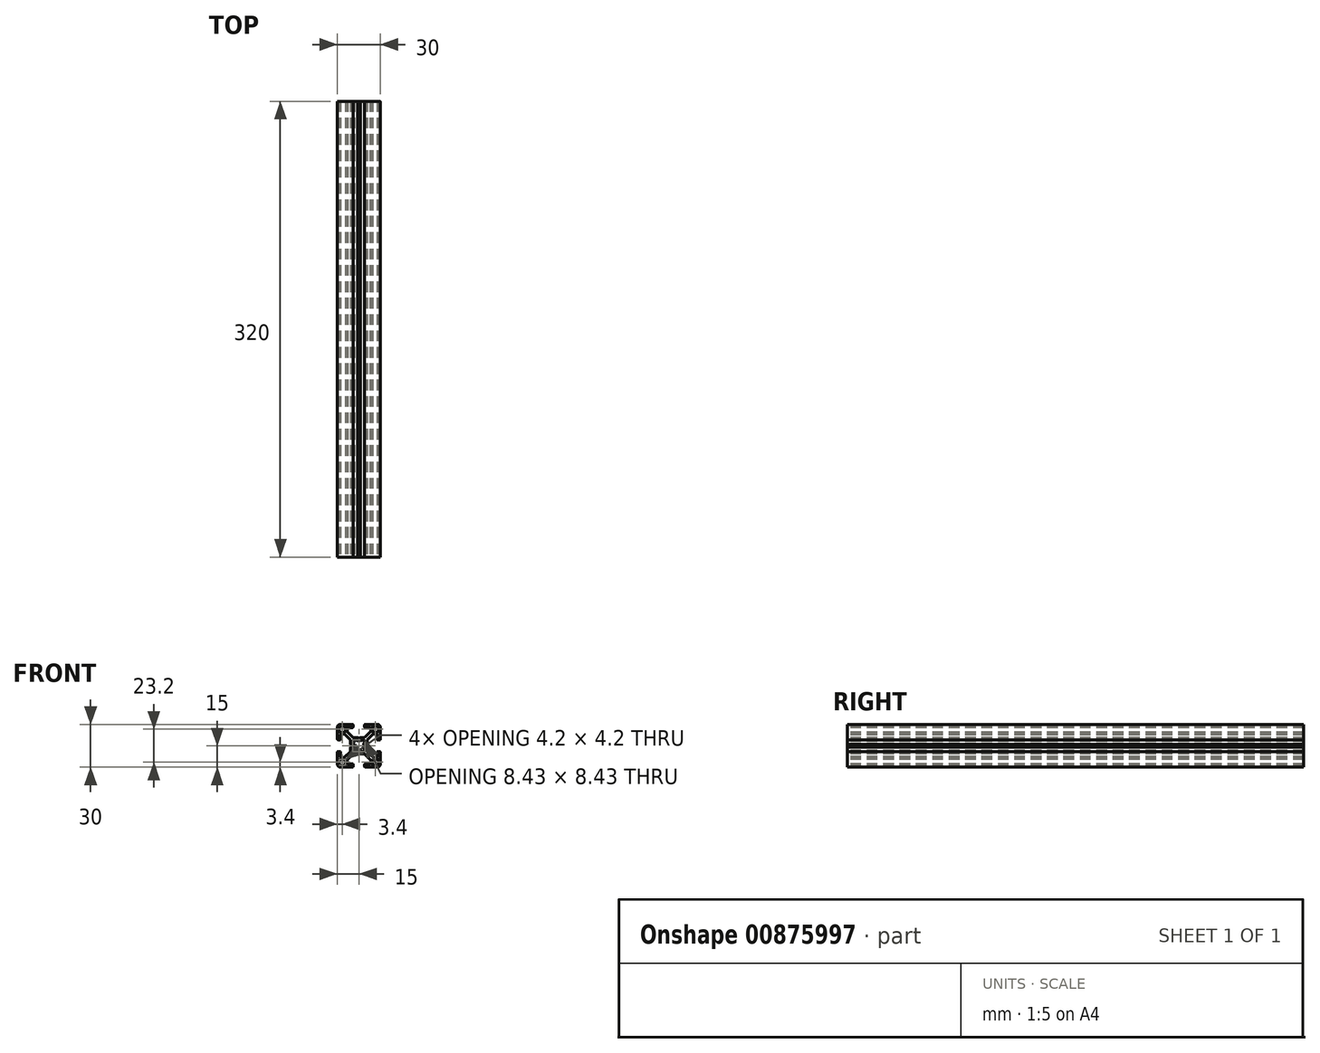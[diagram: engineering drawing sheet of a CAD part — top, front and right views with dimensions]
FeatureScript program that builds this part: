
annotation { "Feature Type Name" : "Feature", "Feature Type Description" : "" }
export const myFeature = defineFeature(function(context is Context, id is Id, definition is map)
    precondition{}
    {
        {
            var Q0;
            Q0=qCreatedBy(makeId("Front.planeOp"),FACE);
            var sketch = newSketch(context, id + "F0", { "sketchPlane" : qUnion([Q0])});
            skArc(sketch, "E0", {"start": v(9.88, 13.7) * mm, "mid": v(9.61, 13.59) * mm, "end": v(9.5, 13.32) * mm});
            skLineSegment(sketch, "E1", {"start": v(12.7, 13.7) * mm, "end": v(9.88, 13.7) * mm});
            skArc(sketch, "E2", {"start": v(13.7, 12.7) * mm, "mid": v(13.4, 13.4) * mm, "end": v(12.7, 13.7) * mm});
            skLineSegment(sketch, "E3", {"start": v(13.7, 9.88) * mm, "end": v(13.7, 12.7) * mm});
            skArc(sketch, "E4", {"start": v(13.32, 9.5) * mm, "mid": v(13.59, 9.61) * mm, "end": v(13.7, 9.88) * mm});
            skLineSegment(sketch, "E5", {"start": v(9.88, 9.5) * mm, "end": v(13.32, 9.5) * mm});
            skArc(sketch, "E6", {"start": v(9.5, 9.88) * mm, "mid": v(9.61, 9.61) * mm, "end": v(9.88, 9.5) * mm});
            skLineSegment(sketch, "E7", {"start": v(9.5, 13.32) * mm, "end": v(9.5, 9.88) * mm});
            skArc(sketch, "E8", {"start": v(-9.5, 13.32) * mm, "mid": v(-9.61, 13.59) * mm, "end": v(-9.88, 13.7) * mm});
            skLineSegment(sketch, "E9", {"start": v(-9.5, 9.88) * mm, "end": v(-9.5, 13.32) * mm});
            skArc(sketch, "E10", {"start": v(-9.88, 9.5) * mm, "mid": v(-9.61, 9.61) * mm, "end": v(-9.5, 9.88) * mm});
            skLineSegment(sketch, "E11", {"start": v(-13.32, 9.5) * mm, "end": v(-9.88, 9.5) * mm});
            skArc(sketch, "E12", {"start": v(-13.7, 9.88) * mm, "mid": v(-13.59, 9.61) * mm, "end": v(-13.32, 9.5) * mm});
            skLineSegment(sketch, "E13", {"start": v(-13.7, 12.7) * mm, "end": v(-13.7, 9.88) * mm});
            skArc(sketch, "E14", {"start": v(-12.7, 13.7) * mm, "mid": v(-13.4, 13.4) * mm, "end": v(-13.7, 12.7) * mm});
            skLineSegment(sketch, "E15", {"start": v(-9.88, 13.7) * mm, "end": v(-12.7, 13.7) * mm});
            skArc(sketch, "E16", {"start": v(-1.5, -3.2) * mm, "mid": v(0, -3.53) * mm, "end": v(1.5, -3.2) * mm});
            skLineSegment(sketch, "E17", {"start": v(-2.47, -3.98) * mm, "end": v(-1.5, -3.2) * mm});
            skArc(sketch, "E18", {"start": v(-3.98, -2.47) * mm, "mid": v(-3.9, -3.9) * mm, "end": v(-2.47, -3.98) * mm});
            skLineSegment(sketch, "E19", {"start": v(-3.2, -1.5) * mm, "end": v(-3.98, -2.47) * mm});
            skArc(sketch, "E20", {"start": v(-3.2, 1.5) * mm, "mid": v(-3.53, 0) * mm, "end": v(-3.2, -1.5) * mm});
            skLineSegment(sketch, "E21", {"start": v(-3.98, 2.47) * mm, "end": v(-3.2, 1.5) * mm});
            skArc(sketch, "E22", {"start": v(-2.47, 3.98) * mm, "mid": v(-3.9, 3.9) * mm, "end": v(-3.98, 2.47) * mm});
            skLineSegment(sketch, "E23", {"start": v(-1.5, 3.2) * mm, "end": v(-2.47, 3.98) * mm});
            skArc(sketch, "E24", {"start": v(1.5, 3.2) * mm, "mid": v(0, 3.53) * mm, "end": v(-1.5, 3.2) * mm});
            skLineSegment(sketch, "E25", {"start": v(2.47, 3.98) * mm, "end": v(1.5, 3.2) * mm});
            skArc(sketch, "E26", {"start": v(3.98, 2.47) * mm, "mid": v(3.9, 3.9) * mm, "end": v(2.47, 3.98) * mm});
            skLineSegment(sketch, "E27", {"start": v(3.2, 1.5) * mm, "end": v(3.98, 2.47) * mm});
            skArc(sketch, "E28", {"start": v(3.2, -1.5) * mm, "mid": v(3.53, 0) * mm, "end": v(3.2, 1.5) * mm});
            skLineSegment(sketch, "E29", {"start": v(3.98, -2.47) * mm, "end": v(3.2, -1.5) * mm});
            skArc(sketch, "E30", {"start": v(2.47, -3.98) * mm, "mid": v(3.9, -3.9) * mm, "end": v(3.98, -2.47) * mm});
            skLineSegment(sketch, "E31", {"start": v(1.5, -3.2) * mm, "end": v(2.47, -3.98) * mm});
            skArc(sketch, "E32", {"start": v(-13.32, -9.5) * mm, "mid": v(-13.59, -9.61) * mm, "end": v(-13.7, -9.88) * mm});
            skLineSegment(sketch, "E33", {"start": v(-9.88, -9.5) * mm, "end": v(-13.32, -9.5) * mm});
            skArc(sketch, "E34", {"start": v(-9.5, -9.88) * mm, "mid": v(-9.61, -9.61) * mm, "end": v(-9.88, -9.5) * mm});
            skLineSegment(sketch, "E35", {"start": v(-9.5, -13.32) * mm, "end": v(-9.5, -9.88) * mm});
            skArc(sketch, "E36", {"start": v(-9.88, -13.7) * mm, "mid": v(-9.61, -13.59) * mm, "end": v(-9.5, -13.32) * mm});
            skLineSegment(sketch, "E37", {"start": v(-12.7, -13.7) * mm, "end": v(-9.88, -13.7) * mm});
            skArc(sketch, "E38", {"start": v(-13.7, -12.7) * mm, "mid": v(-13.4, -13.4) * mm, "end": v(-12.7, -13.7) * mm});
            skLineSegment(sketch, "E39", {"start": v(-13.7, -9.88) * mm, "end": v(-13.7, -12.7) * mm});
            skArc(sketch, "E40", {"start": v(9.5, -13.32) * mm, "mid": v(9.61, -13.59) * mm, "end": v(9.88, -13.7) * mm});
            skLineSegment(sketch, "E41", {"start": v(9.5, -9.88) * mm, "end": v(9.5, -13.32) * mm});
            skArc(sketch, "E42", {"start": v(9.88, -9.5) * mm, "mid": v(9.61, -9.61) * mm, "end": v(9.5, -9.88) * mm});
            skLineSegment(sketch, "E43", {"start": v(13.32, -9.5) * mm, "end": v(9.88, -9.5) * mm});
            skArc(sketch, "E44", {"start": v(13.7, -9.88) * mm, "mid": v(13.59, -9.61) * mm, "end": v(13.32, -9.5) * mm});
            skLineSegment(sketch, "E45", {"start": v(13.7, -12.7) * mm, "end": v(13.7, -9.88) * mm});
            skArc(sketch, "E46", {"start": v(12.7, -13.7) * mm, "mid": v(13.4, -13.4) * mm, "end": v(13.7, -12.7) * mm});
            skLineSegment(sketch, "E47", {"start": v(9.88, -13.7) * mm, "end": v(12.7, -13.7) * mm});
            skArc(sketch, "E48", {"start": v(13.24, -4) * mm, "mid": v(12.89, -4.15) * mm, "end": v(12.74, -4.5) * mm});
            skLineSegment(sketch, "E49", {"start": v(12.74, -4.5) * mm, "end": v(12.74, -7.73) * mm});
            skArc(sketch, "E50", {"start": v(12.24, -8.25) * mm, "mid": v(12.6, -8.1) * mm, "end": v(12.74, -7.73) * mm});
            skLineSegment(sketch, "E51", {"start": v(12.24, -8.25) * mm, "end": v(10.26, -8.25) * mm});
            skArc(sketch, "E52", {"start": v(9.9, -8.1) * mm, "mid": v(10.07, -8.21) * mm, "end": v(10.26, -8.25) * mm});
            skLineSegment(sketch, "E53", {"start": v(9.9, -8.1) * mm, "end": v(5.98, -4.18) * mm});
            skArc(sketch, "E54", {"start": v(5.83, -3.82) * mm, "mid": v(5.87, -4.02) * mm, "end": v(5.98, -4.18) * mm});
            skLineSegment(sketch, "E55", {"start": v(5.83, -3.82) * mm, "end": v(5.83, -1.01) * mm});
            skLineSegment(sketch, "E56", {"start": v(5.83, -1.01) * mm, "end": v(5.32, -0.06) * mm});
            skLineSegment(sketch, "E57", {"start": v(5.32, -0.06) * mm, "end": v(5.83, 0.89) * mm});
            skLineSegment(sketch, "E58", {"start": v(5.83, 0.89) * mm, "end": v(5.83, 3.82) * mm});
            skArc(sketch, "E59", {"start": v(5.98, 4.18) * mm, "mid": v(5.87, 4.02) * mm, "end": v(5.83, 3.82) * mm});
            skLineSegment(sketch, "E60", {"start": v(5.98, 4.18) * mm, "end": v(9.9, 8.1) * mm});
            skArc(sketch, "E61", {"start": v(10.26, 8.25) * mm, "mid": v(10.07, 8.21) * mm, "end": v(9.9, 8.1) * mm});
            skLineSegment(sketch, "E62", {"start": v(10.26, 8.25) * mm, "end": v(12.24, 8.25) * mm});
            skArc(sketch, "E63", {"start": v(12.74, 7.73) * mm, "mid": v(12.6, 8.1) * mm, "end": v(12.24, 8.25) * mm});
            skLineSegment(sketch, "E64", {"start": v(12.74, 7.73) * mm, "end": v(12.74, 4.5) * mm});
            skArc(sketch, "E65", {"start": v(12.74, 4.5) * mm, "mid": v(12.89, 4.15) * mm, "end": v(13.24, 4) * mm});
            skLineSegment(sketch, "E66", {"start": v(13.24, 4) * mm, "end": v(14.5, 4) * mm});
            skArc(sketch, "E67", {"start": v(14.5, 4) * mm, "mid": v(14.85, 4.15) * mm, "end": v(15, 4.5) * mm});
            skLineSegment(sketch, "E68", {"start": v(15, 4.5) * mm, "end": v(15, 13) * mm});
            skArc(sketch, "E69", {"start": v(15, 13) * mm, "mid": v(14.41, 14.41) * mm, "end": v(13, 15) * mm});
            skLineSegment(sketch, "E70", {"start": v(13, 15) * mm, "end": v(4.5, 15) * mm});
            skArc(sketch, "E71", {"start": v(4.5, 15) * mm, "mid": v(4.15, 14.85) * mm, "end": v(4, 14.5) * mm});
            skLineSegment(sketch, "E72", {"start": v(4, 14.5) * mm, "end": v(4, 13.24) * mm});
            skArc(sketch, "E73", {"start": v(4, 13.24) * mm, "mid": v(4.15, 12.89) * mm, "end": v(4.5, 12.74) * mm});
            skLineSegment(sketch, "E74", {"start": v(4.5, 12.74) * mm, "end": v(7.73, 12.74) * mm});
            skArc(sketch, "E75", {"start": v(8.25, 12.24) * mm, "mid": v(8.1, 12.6) * mm, "end": v(7.73, 12.74) * mm});
            skLineSegment(sketch, "E76", {"start": v(8.25, 12.24) * mm, "end": v(8.25, 10.26) * mm});
            skArc(sketch, "E77", {"start": v(8.1, 9.9) * mm, "mid": v(8.21, 10.07) * mm, "end": v(8.25, 10.26) * mm});
            skLineSegment(sketch, "E78", {"start": v(8.1, 9.9) * mm, "end": v(4.18, 5.98) * mm});
            skArc(sketch, "E79", {"start": v(3.82, 5.83) * mm, "mid": v(4.02, 5.87) * mm, "end": v(4.18, 5.98) * mm});
            skLineSegment(sketch, "E80", {"start": v(3.82, 5.83) * mm, "end": v(0.95, 5.83) * mm});
            skLineSegment(sketch, "E81", {"start": v(0.95, 5.83) * mm, "end": v(0, 5.32) * mm});
            skLineSegment(sketch, "E82", {"start": v(0, 5.32) * mm, "end": v(-0.95, 5.83) * mm});
            skLineSegment(sketch, "E83", {"start": v(-0.95, 5.83) * mm, "end": v(-3.82, 5.83) * mm});
            skArc(sketch, "E84", {"start": v(-4.18, 5.98) * mm, "mid": v(-4.02, 5.87) * mm, "end": v(-3.82, 5.83) * mm});
            skLineSegment(sketch, "E85", {"start": v(-4.18, 5.98) * mm, "end": v(-8.1, 9.9) * mm});
            skArc(sketch, "E86", {"start": v(-8.25, 10.26) * mm, "mid": v(-8.21, 10.07) * mm, "end": v(-8.1, 9.9) * mm});
            skLineSegment(sketch, "E87", {"start": v(-8.25, 10.26) * mm, "end": v(-8.25, 12.24) * mm});
            skArc(sketch, "E88", {"start": v(-7.73, 12.74) * mm, "mid": v(-8.1, 12.6) * mm, "end": v(-8.25, 12.24) * mm});
            skLineSegment(sketch, "E89", {"start": v(-7.73, 12.74) * mm, "end": v(-4.5, 12.74) * mm});
            skArc(sketch, "E90", {"start": v(-4.5, 12.74) * mm, "mid": v(-4.15, 12.89) * mm, "end": v(-4, 13.24) * mm});
            skLineSegment(sketch, "E91", {"start": v(-4, 13.24) * mm, "end": v(-4, 14.5) * mm});
            skArc(sketch, "E92", {"start": v(-4, 14.5) * mm, "mid": v(-4.15, 14.85) * mm, "end": v(-4.5, 15) * mm});
            skLineSegment(sketch, "E93", {"start": v(-4.5, 15) * mm, "end": v(-13, 15) * mm});
            skArc(sketch, "E94", {"start": v(-13, 15) * mm, "mid": v(-14.41, 14.41) * mm, "end": v(-15, 13) * mm});
            skLineSegment(sketch, "E95", {"start": v(-15, 13) * mm, "end": v(-15, 4.5) * mm});
            skArc(sketch, "E96", {"start": v(-15, 4.5) * mm, "mid": v(-14.85, 4.15) * mm, "end": v(-14.5, 4) * mm});
            skLineSegment(sketch, "E97", {"start": v(-14.5, 4) * mm, "end": v(-13.24, 4) * mm});
            skArc(sketch, "E98", {"start": v(-13.24, 4) * mm, "mid": v(-12.89, 4.15) * mm, "end": v(-12.74, 4.5) * mm});
            skLineSegment(sketch, "E99", {"start": v(-12.74, 4.5) * mm, "end": v(-12.74, 7.73) * mm});
            skArc(sketch, "E100", {"start": v(-12.24, 8.25) * mm, "mid": v(-12.6, 8.1) * mm, "end": v(-12.74, 7.73) * mm});
            skLineSegment(sketch, "E101", {"start": v(-12.24, 8.25) * mm, "end": v(-10.26, 8.25) * mm});
            skArc(sketch, "E102", {"start": v(-9.9, 8.1) * mm, "mid": v(-10.07, 8.21) * mm, "end": v(-10.26, 8.25) * mm});
            skLineSegment(sketch, "E103", {"start": v(-9.9, 8.1) * mm, "end": v(-5.98, 4.18) * mm});
            skArc(sketch, "E104", {"start": v(-5.83, 3.82) * mm, "mid": v(-5.87, 4.02) * mm, "end": v(-5.98, 4.18) * mm});
            skLineSegment(sketch, "E105", {"start": v(-5.83, 3.82) * mm, "end": v(-5.83, 0.89) * mm});
            skLineSegment(sketch, "E106", {"start": v(-5.83, 0.89) * mm, "end": v(-5.32, -0.06) * mm});
            skLineSegment(sketch, "E107", {"start": v(-5.32, -0.06) * mm, "end": v(-5.83, -1.01) * mm});
            skLineSegment(sketch, "E108", {"start": v(-5.83, -1.01) * mm, "end": v(-5.83, -3.82) * mm});
            skArc(sketch, "E109", {"start": v(-5.98, -4.18) * mm, "mid": v(-5.87, -4.02) * mm, "end": v(-5.83, -3.82) * mm});
            skLineSegment(sketch, "E110", {"start": v(-5.98, -4.18) * mm, "end": v(-9.9, -8.1) * mm});
            skArc(sketch, "E111", {"start": v(-10.26, -8.25) * mm, "mid": v(-10.07, -8.21) * mm, "end": v(-9.9, -8.1) * mm});
            skLineSegment(sketch, "E112", {"start": v(-10.26, -8.25) * mm, "end": v(-12.24, -8.25) * mm});
            skArc(sketch, "E113", {"start": v(-12.74, -7.73) * mm, "mid": v(-12.6, -8.1) * mm, "end": v(-12.24, -8.25) * mm});
            skLineSegment(sketch, "E114", {"start": v(-12.74, -7.73) * mm, "end": v(-12.74, -4.5) * mm});
            skArc(sketch, "E115", {"start": v(-12.74, -4.5) * mm, "mid": v(-12.89, -4.15) * mm, "end": v(-13.24, -4) * mm});
            skLineSegment(sketch, "E116", {"start": v(-13.24, -4) * mm, "end": v(-14.5, -4) * mm});
            skArc(sketch, "E117", {"start": v(-14.5, -4) * mm, "mid": v(-14.85, -4.15) * mm, "end": v(-15, -4.5) * mm});
            skLineSegment(sketch, "E118", {"start": v(-15, -4.5) * mm, "end": v(-15, -13) * mm});
            skArc(sketch, "E119", {"start": v(-15, -13) * mm, "mid": v(-14.41, -14.41) * mm, "end": v(-13, -15) * mm});
            skLineSegment(sketch, "E120", {"start": v(-13, -15) * mm, "end": v(-4.5, -15) * mm});
            skArc(sketch, "E121", {"start": v(-4.5, -15) * mm, "mid": v(-4.15, -14.85) * mm, "end": v(-4, -14.5) * mm});
            skLineSegment(sketch, "E122", {"start": v(-4, -14.5) * mm, "end": v(-4, -13.24) * mm});
            skArc(sketch, "E123", {"start": v(-4, -13.24) * mm, "mid": v(-4.15, -12.89) * mm, "end": v(-4.5, -12.74) * mm});
            skLineSegment(sketch, "E124", {"start": v(-4.5, -12.74) * mm, "end": v(-7.73, -12.74) * mm});
            skArc(sketch, "E125", {"start": v(-8.25, -12.24) * mm, "mid": v(-8.1, -12.6) * mm, "end": v(-7.73, -12.74) * mm});
            skLineSegment(sketch, "E126", {"start": v(-8.25, -12.24) * mm, "end": v(-8.25, -10.26) * mm});
            skArc(sketch, "E127", {"start": v(-8.1, -9.9) * mm, "mid": v(-8.21, -10.07) * mm, "end": v(-8.25, -10.26) * mm});
            skLineSegment(sketch, "E128", {"start": v(-8.1, -9.9) * mm, "end": v(-4.18, -5.98) * mm});
            skArc(sketch, "E129", {"start": v(-3.82, -5.83) * mm, "mid": v(-4.02, -5.87) * mm, "end": v(-4.18, -5.98) * mm});
            skLineSegment(sketch, "E130", {"start": v(-3.82, -5.83) * mm, "end": v(-0.95, -5.83) * mm});
            skLineSegment(sketch, "E131", {"start": v(-0.95, -5.83) * mm, "end": v(0, -5.32) * mm});
            skLineSegment(sketch, "E132", {"start": v(0, -5.32) * mm, "end": v(0.95, -5.83) * mm});
            skLineSegment(sketch, "E133", {"start": v(0.95, -5.83) * mm, "end": v(3.82, -5.83) * mm});
            skArc(sketch, "E134", {"start": v(4.18, -5.98) * mm, "mid": v(4.02, -5.87) * mm, "end": v(3.82, -5.83) * mm});
            skLineSegment(sketch, "E135", {"start": v(4.18, -5.98) * mm, "end": v(8.1, -9.9) * mm});
            skArc(sketch, "E136", {"start": v(8.25, -10.26) * mm, "mid": v(8.21, -10.07) * mm, "end": v(8.1, -9.9) * mm});
            skLineSegment(sketch, "E137", {"start": v(8.25, -10.26) * mm, "end": v(8.25, -12.24) * mm});
            skArc(sketch, "E138", {"start": v(7.73, -12.74) * mm, "mid": v(8.1, -12.6) * mm, "end": v(8.25, -12.24) * mm});
            skLineSegment(sketch, "E139", {"start": v(7.73, -12.74) * mm, "end": v(4.5, -12.74) * mm});
            skArc(sketch, "E140", {"start": v(4.5, -12.74) * mm, "mid": v(4.15, -12.89) * mm, "end": v(4, -13.24) * mm});
            skLineSegment(sketch, "E141", {"start": v(4, -13.24) * mm, "end": v(4, -14.5) * mm});
            skArc(sketch, "E142", {"start": v(4, -14.5) * mm, "mid": v(4.15, -14.85) * mm, "end": v(4.5, -15) * mm});
            skLineSegment(sketch, "E143", {"start": v(4.5, -15) * mm, "end": v(13, -15) * mm});
            skArc(sketch, "E144", {"start": v(13, -15) * mm, "mid": v(14.41, -14.41) * mm, "end": v(15, -13) * mm});
            skLineSegment(sketch, "E145", {"start": v(15, -13) * mm, "end": v(15, -4.5) * mm});
            skArc(sketch, "E146", {"start": v(15, -4.5) * mm, "mid": v(14.85, -4.15) * mm, "end": v(14.5, -4) * mm});
            skLineSegment(sketch, "E147", {"start": v(14.5, -4) * mm, "end": v(13.24, -4) * mm});
            skSolve(sketch);
        }
        {
            var Q0;
            Q0=qCreatedBy(makeId("Top.planeOp"),FACE);
            var sketch = newSketch(context, id + "F1", { "sketchPlane" : qUnion([Q0])});
            skLineSegment(sketch, "E148", {"start": v(-1.5, 160) * mm, "end": v(-1.5, -160) * mm});
            skSolve(sketch);
        }
        {
            var Q0;
            Q0=qSketchRegion(id+"F0",true);
            var Q1;
            Q1=sQuery(id+"F1.wireOp",EDGE,"E148");
            var Q2;
            Q2=sQuery(id+"F1.wireOp",EDGE,"fSjTIPXa-SZZ6-Uh3d-dTjF-iSAX6K3vTkU0");
            var Q3;
            Q3=sQuery(id+"F1.wireOp",EDGE,"X1iaMUp9-18Uv-Qplb-D4Eo-NhRo6oMLb04g");
            var Q4;
            Q4=sQuery(id+"F1.wireOp",EDGE,"ysMRVMGi-oqtn-a0SZ-pmm6-otZbrj3hBrry");
            sweep(context, id + "F2", {"profiles" : qUnion([Q0]), "path" : qUnion([Q1, Q2, Q3, Q4])});
        }
    });
